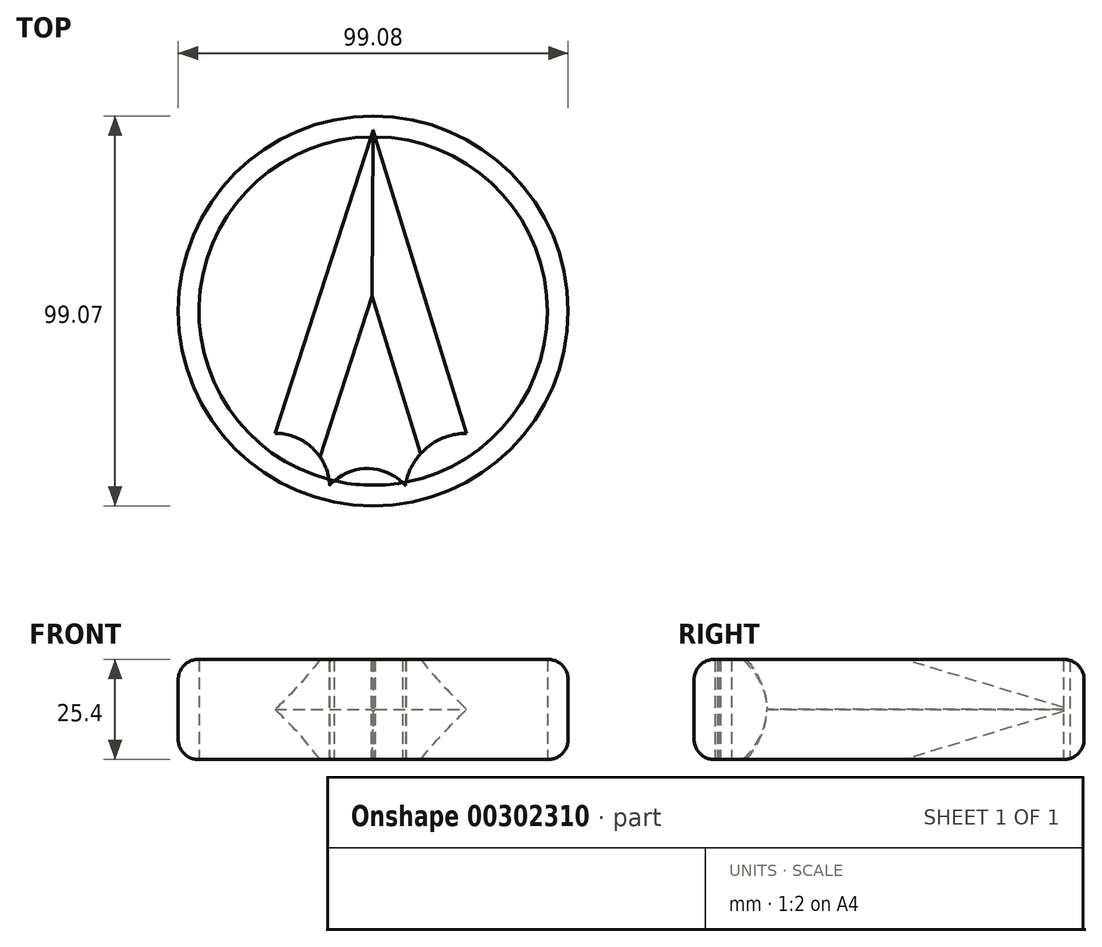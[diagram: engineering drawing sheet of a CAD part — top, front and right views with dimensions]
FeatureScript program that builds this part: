
annotation { "Feature Type Name" : "Feature", "Feature Type Description" : "" }
export const myFeature = defineFeature(function(context is Context, id is Id, definition is map)
    precondition{}
    {
        {
            var Q0;
            Q0=qCreatedBy(makeId("Top.planeOp"),FACE);
            var sketch = newSketch(context, id + "F0", { "sketchPlane" : qUnion([Q0])});
            skLineSegment(sketch, "E0", {"start": v(0, 76.98) * mm, "end": v(-24.93, 0) * mm});
            skLineSegment(sketch, "E1", {"start": v(0, 76.98) * mm, "end": v(23.78, 0) * mm});
            skLineSegment(sketch, "E2", {"start": v(-24.93, 0) * mm, "end": v(23.78, 0) * mm});
            skArc(sketch, "E3", {"start": v(-11.06, -13.23) * mm, "mid": v(-15.35, -3.84) * mm, "end": v(-24.93, 0) * mm});
            skArc(sketch, "E4", {"start": v(8.16, -13.23) * mm, "mid": v(-1.45, -8.97) * mm, "end": v(-11.06, -13.23) * mm});
            skArc(sketch, "E5", {"start": v(23.78, 0) * mm, "mid": v(13.55, -3.75) * mm, "end": v(8.16, -13.23) * mm});
            skCircle(sketch, "E6", {"center": v(0, 31.05) * mm, "radius": 49.54 * mm});
            skCircle(sketch, "E7", {"center": v(0, 31.05) * mm, "radius": 44.26 * mm});
            skSolve(sketch);
        }
        {
            var Q0;
            Q0=makeQuery(id+"F0.imprint","IMPRINT",FACE,{"disambiguationData":[TD([[makeQuery(id+"F0.imprint","IMPRINT",EDGE,{"derivedFrom":sQuery(id+"F0.wireOp",EDGE,"E6")}),1.0]])]});
            var Q1;
            {var subQ0=sQuery(id+"F0.wireOp",EDGE,"E2");Q1=makeQuery(id+"F0.imprint","IMPRINT",FACE,{"disambiguationData":[TD([[makeQuery(id+"F0.imprint","IMPRINT",EDGE,{"derivedFrom":subQ0}),1.0]])]});}
            var Q2;
            {var subQ1=sQuery(id+"F0.wireOp",EDGE,"E2");Q2=makeQuery(id+"F0.imprint","IMPRINT",FACE,{"disambiguationData":[TD([[makeQuery(id+"F0.imprint","IMPRINT",EDGE,{"derivedFrom":subQ1}),-1.0]])]});}
            extrude(context, id + "F1", {"entities" : qUnion([Q0, Q1, Q2]), "depth" : 25.4 * mm});
        }
        {
            var Q0;
            Q0=makeQuery(id+"F1.opExtrude","CAP_EDGE",EDGE,{"disambiguationData":[OSD([sQuery(id+"F0.wireOp",EDGE,"E6")])],"isStart":false});
            var Q1;
            Q1=makeQuery(id+"F1.opExtrude","CAP_EDGE",EDGE,{"disambiguationData":[OSD([sQuery(id+"F0.wireOp",EDGE,"E6")])],"isStart":true});
            fillet(context, id + "F2", {"entities" : qUnion([Q0, Q1]), "radius" : 5.08 * mm, "tangentPropagation" : true, "allowEdgeOverflow" : false});
        }
        {
            var Q0;
            {var subQ0=sQuery(id+"F0.wireOp",EDGE,"E0");Q0=makeQuery(id+"F1.opExtrude","CAP_EDGE",EDGE,{"disambiguationData":[OSD([subQ0]),TDD([makeQuery(id+"F0.imprint","IMPRINT",EDGE,{"disambiguationData":[TD([[makeQuery(id+"F0.imprint","INTERSECT",VERTEX,{"derivedFrom":[subQ0,sQuery(id+"F0.wireOp",EDGE,"E7")]}),-1.0]])],"derivedFrom":subQ0})])],"isStart":false});}
            var Q1;
            {var subQ0=sQuery(id+"F0.wireOp",EDGE,"E1");Q1=makeQuery(id+"F1.opExtrude","CAP_EDGE",EDGE,{"disambiguationData":[OSD([subQ0]),TDD([makeQuery(id+"F0.imprint","IMPRINT",EDGE,{"disambiguationData":[TD([[makeQuery(id+"F0.imprint","INTERSECT",VERTEX,{"derivedFrom":[subQ0,sQuery(id+"F0.wireOp",EDGE,"E7")]}),-1.0]])],"derivedFrom":subQ0})])],"isStart":false});}
            var Q2;
            {var subQ0=sQuery(id+"F0.wireOp",EDGE,"E1");Q2=makeQuery(id+"F1.opExtrude","CAP_EDGE",EDGE,{"disambiguationData":[OSD([subQ0]),TDD([makeQuery(id+"F0.imprint","IMPRINT",EDGE,{"disambiguationData":[TD([[makeQuery(id+"F0.imprint","INTERSECT",VERTEX,{"derivedFrom":[subQ0,sQuery(id+"F0.wireOp",EDGE,"E7")]}),-1.0]])],"derivedFrom":subQ0})])],"isStart":true});}
            var Q3;
            {var subQ0=sQuery(id+"F0.wireOp",EDGE,"E0");Q3=makeQuery(id+"F1.opExtrude","CAP_EDGE",EDGE,{"disambiguationData":[OSD([subQ0]),TDD([makeQuery(id+"F0.imprint","IMPRINT",EDGE,{"disambiguationData":[TD([[makeQuery(id+"F0.imprint","INTERSECT",VERTEX,{"derivedFrom":[subQ0,sQuery(id+"F0.wireOp",EDGE,"E7")]}),-1.0]])],"derivedFrom":subQ0})])],"isStart":true});}
            chamfer(context, id + "F3", {"entities" : qUnion([Q0, Q1, Q2, Q3]), "width" : 12.7 * mm, "tangentPropagation" : true});
        }
    });
